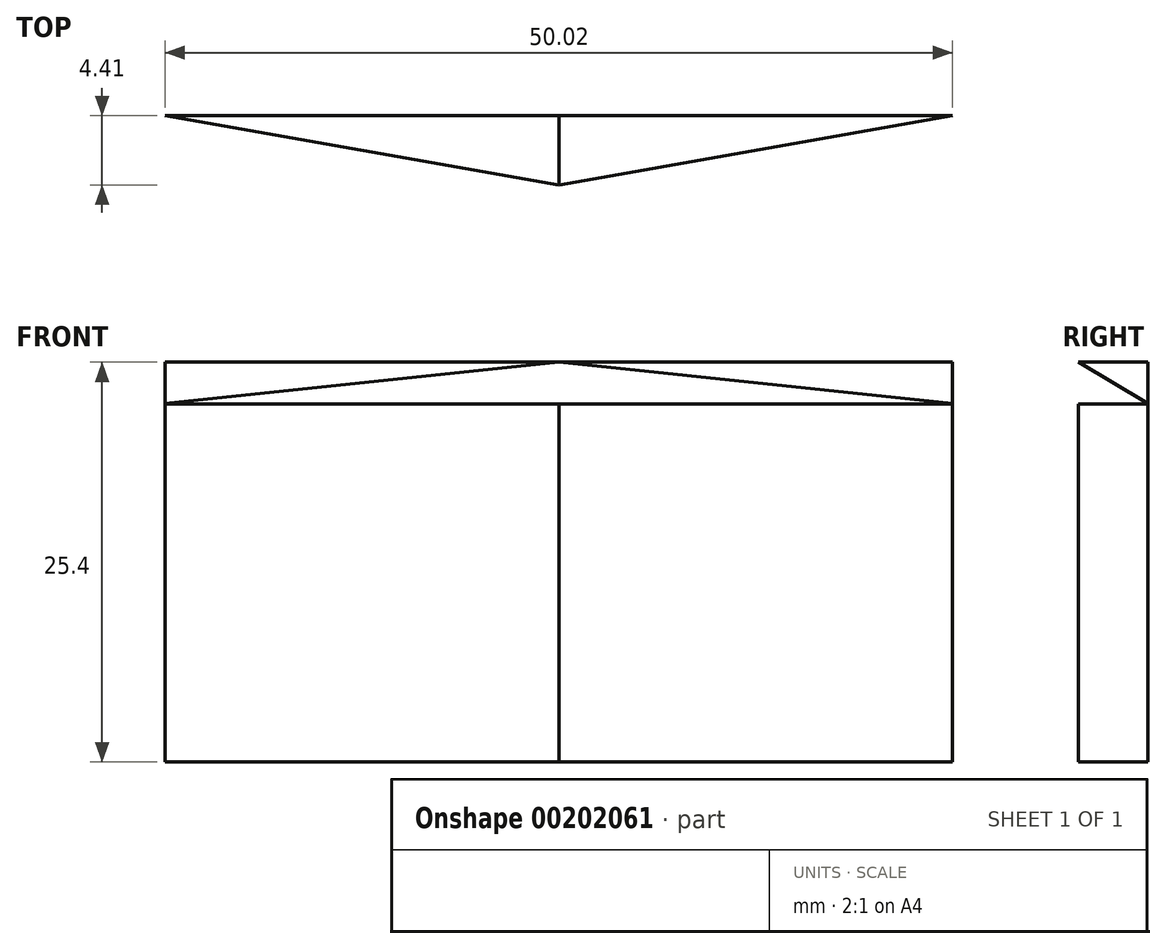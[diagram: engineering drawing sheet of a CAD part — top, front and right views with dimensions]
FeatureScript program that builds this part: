
annotation { "Feature Type Name" : "Feature", "Feature Type Description" : "" }
export const myFeature = defineFeature(function(context is Context, id is Id, definition is map)
    precondition{}
    {
        {
            var Q0;
            Q0=qCreatedBy(makeId("Top.planeOp"),FACE);
            var sketch = newSketch(context, id + "F0", { "sketchPlane" : qUnion([Q0])});
            skLineSegment(sketch, "E0", {"start": v(0, 0) * mm, "end": v(25.01, 4.41) * mm});
            skLineSegment(sketch, "E1", {"start": v(0, 0) * mm, "end": v(-76.2, 0) * mm});
            skLineSegment(sketch, "E2", {"start": v(0, 0) * mm, "end": v(76.2, 0) * mm});
            skLineSegment(sketch, "E3", {"start": v(0, 0) * mm, "end": v(-25.01, 4.41) * mm});
            skLineSegment(sketch, "E4", {"start": v(-25.01, 4.41) * mm, "end": v(25.01, 4.41) * mm});
            skSolve(sketch);
        }
        {
            var Q0;
            Q0=qCreatedBy(makeId("Front.planeOp"),FACE);
            var sketch = newSketch(context, id + "F1", { "sketchPlane" : qUnion([Q0])});
            skLineSegment(sketch, "E5", {"start": v(0, 0) * mm, "end": v(25.4, -2.67) * mm});
            skLineSegment(sketch, "E6", {"start": v(25.4, -2.67) * mm, "end": v(-25.4, -2.67) * mm});
            skLineSegment(sketch, "E7", {"start": v(0, 0) * mm, "end": v(-25.4, -2.67) * mm});
            skSolve(sketch);
        }
        {
            var Q0;
            Q0 = qSketchRegion(id + "F0", true);
            extrude(context, id + "F2", {"entities" : qUnion([Q0]), "oppositeDirection" : true, "depth" : 25.4 * mm});
        }
        {
            var Q0;
            Q0 = qSketchRegion(id + "F1", true);
            extrude(context, id + "F3", {"entities" : qUnion([Q0]), "operationType" : NewBodyOperationType.REMOVE, "oppositeDirection" : true, "depth" : 25.4 * mm});
        }
    });
